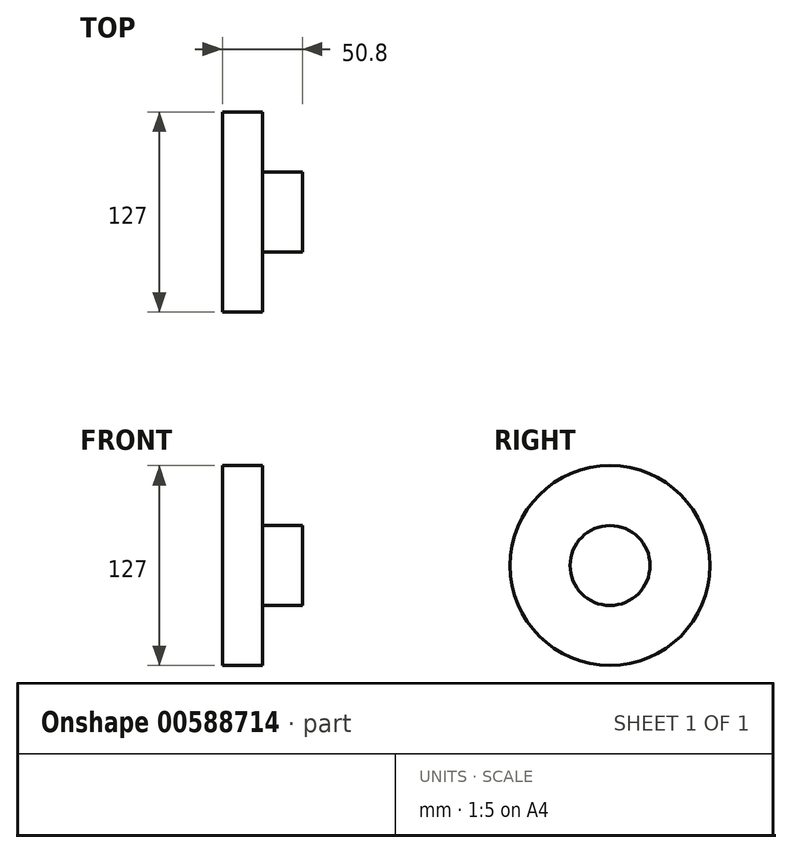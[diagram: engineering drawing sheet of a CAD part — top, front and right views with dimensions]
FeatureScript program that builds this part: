
annotation { "Feature Type Name" : "Feature", "Feature Type Description" : "" }
export const myFeature = defineFeature(function(context is Context, id is Id, definition is map)
    precondition{}
    {
        {
            var Q0;
            Q0=qCreatedBy(makeId("Front.planeOp"),FACE);
            var sketch = newSketch(context, id + "F0", { "sketchPlane" : qUnion([Q0])});
            skLineSegment(sketch, "E0", {"start": v(0, 63.5) * mm, "end": v(0, 0) * mm});
            skLineSegment(sketch, "E1", {"start": v(0, 0) * mm, "end": v(50.8, 0) * mm});
            skLineSegment(sketch, "E2", {"start": v(50.8, 0) * mm, "end": v(50.8, 25.4) * mm});
            skLineSegment(sketch, "E3", {"start": v(50.8, 25.4) * mm, "end": v(25.4, 25.4) * mm});
            skLineSegment(sketch, "E4", {"start": v(0, 63.5) * mm, "end": v(25.4, 63.5) * mm});
            skLineSegment(sketch, "E5", {"start": v(25.4, 63.5) * mm, "end": v(25.4, 25.4) * mm});
            skSolve(sketch);
        }
        {
            var Q0;
            Q0 = qSketchRegion(id + "F0", true);
            var Q1;
            Q1=sQuery(id+"F0.wireOp",EDGE,"E1");
            revolve(context, id + "F1", {"entities" : qUnion([Q0]), "axis" : qUnion([Q1]), "revolveType" : RevolveType.FULL});
        }
    });
